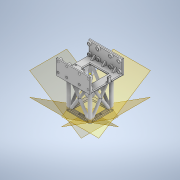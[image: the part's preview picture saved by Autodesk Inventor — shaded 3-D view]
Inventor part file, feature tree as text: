
AUTODESK INVENTOR PART (.ipt)
format: ipt  version: 2020 (Build 240168000, 168)  size: 669,184 bytes
history: native  units: in
note: dims shown in document units (in); Inventor stores cm internally (conversion verified against a paired STEP export)
features: sketch x15, extrude x14, plane x8, mirror x4, fillet x3, chamfer x1, pattern_circular x1
ambient origin geometry x8: Origin, YZ Plane, XZ Plane, XY Plane, X Axis, Y Axis, Z Axis, Center Point
bodies: Solid1 (feature_tree)
feature tree (46):
  extrude  "Extrusion1"  Depth=0.1969in TaperAngle=0.0deg
  extrude  "Extrusion2"  Depth=0.1969in
  extrude  "Extrusion3"  Depth=2.0079in
  extrude  "Extrusion4"  Depth=0.2362in
  mirror  "Mirror1"
  mirror  "Mirror2"
  extrude  "Extrusion5"  Depth=0.2362in
  extrude  "Extrusion6"  Depth=5.9055in TaperAngle=0.0deg
  extrude  "Extrusion7"  Depth=0.3937in
  sketch  "Sketch8"  dims[d18=0.3937in d19=0.3937in d20=0.3937in d21=0.0in]
  extrude  "Extrusion8"  Depth=0.3937in
  chamfer  "Chamfer1"  Distance=0.3937in
  mirror  "Mirror3"
  extrude  "Extrusion9"  Depth=0.1969in
  extrude  "Extrusion10"  Depth=0.0591in
  plane  "Work Plane1"
  extrude  "Extrusion11"  TaperAngle=135.0deg  [1 undecoded]
  mirror  "Mirror4"
  pattern_circular  "Circular Pattern1"  [2 undecoded]
  extrude  "Extrusion12"  TaperAngle=90.0deg  [1 undecoded]
  extrude  "Extrusion13"  TaperAngle=90.0deg  [1 undecoded]
  fillet  "Fillet1"  Radius=0.8268in
  extrude  "Extrusion14"  TaperAngle=0.0deg  [1 undecoded]
  fillet  "Fillet2"  Radius=0.8268in
  fillet  "Fillet3"  Radius=0.4134in
  sketch  "Sketch1"  dims[d1=4.0157in d2=0.1969in d3=0.0in]
  sketch  "Sketch2"  dims[d4=0.1969in d5=0.1969in]
  sketch  "Sketch3"  dims[d6=1.5748in d7=0.0in d8=2.0079in]
  sketch  "Sketch4"  dims[d9=2.0079in d10=0.2362in]
  sketch  "Sketch5"  dims[d11=0.2362in d12=0.2362in]
  sketch  "Sketch6"  dims[d13=0.2362in d14=5.9055in d15=0.0in]
  sketch  "Sketch7"  dims[d16=0.3937in d17=0.3937in]
  sketch  "Sketch9"  dims[d23=0.1969in d24=0.0591in]
  sketch  "Sketch10"  dims[d25=45.0deg d26=0.0591in]
  sketch  "Sketch11"  dims[d27=90.0deg d28=135.0deg]
  sketch  "Sketch12"  dims[d29=0.0591in]
  plane  "Work Plane2"
  plane  "Work Plane3"
  plane  "Work Plane4"
  plane  "Work Plane5"
  plane  "Work Plane6"
  plane  "Work Plane7"
  plane  "Work Plane8"
  sketch  "Sketch13"  dims[d30=45.0deg]
  sketch  "Sketch14"  dims[d31=0.0591in]
  sketch  "Sketch15"  dims[d32=90.0deg d33=0.0591in d34=90.0deg d35=90.0deg d36=0.8268in d37=0.0in d38=0.0in d39=0.8268in d40=0.0in d41=0.4134in d42=0.4134in d43=0.1575in d44=0.1575in d45=0.8268in d46=0.0in d47=0.1969in d48=0.3937in d49=0.1969in d50=0.3937in d51=0.1969in d52=0.3937in d53=0.0in d54=0.3937in d55=0.0787in d56=45.0deg d58=0.3937in d59=0.3937in d60=0.3937in d61=0.3937in d62=3.7402in d63=0.0in d64=0.748in d65=0.748in d66=0.748in d67=0.748in d68=0.3937in d69=0.1969in d70=0.0in d71=0.2233in d72=0.2953in d73=4.0551in d74=0.0984in d75=0.0in d76=0.0in d77=1.5748in d78=360.0deg d80=4.0551in d81=0.0in d82=0.1575in d83=0.1575in d84=0.1575in d85=0.1575in d86=0.3937in d87=0.0in d88=0.0787in d89=0.1969in d90=0.3937in d91=0.5906in d92=0.0984in d93=0.0in d94=0.0in d95=0.0787in d96=0.1181in]
note: 6 required parameter values undecoded (feature->parameter linkage not recoverable at this tier; creation-order binding heuristic only, values carry confidence <= 0.55)
